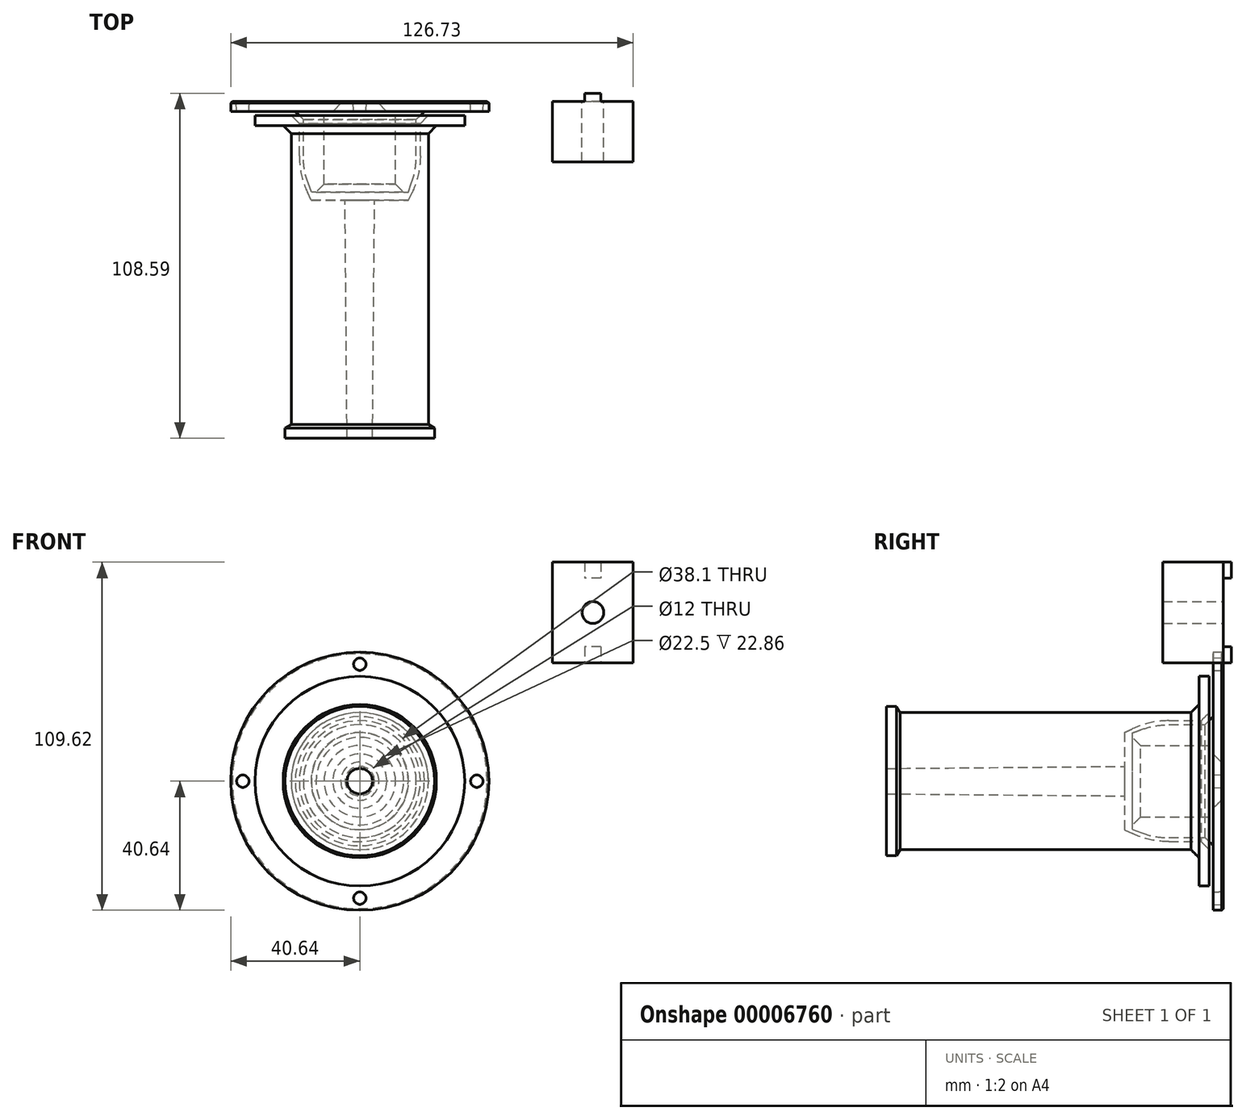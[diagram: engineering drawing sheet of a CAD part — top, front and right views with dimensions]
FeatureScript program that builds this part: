
annotation { "Feature Type Name" : "Feature", "Feature Type Description" : "" }
export const myFeature = defineFeature(function(context is Context, id is Id, definition is map)
    precondition{}
    {
        {
            var Q0;
            Q0=qCreatedBy(makeId("Front.planeOp"),FACE);
            var sketch = newSketch(context, id + "F0", { "sketchPlane" : qUnion([Q0])});
            skCircle(sketch, "E0", {"center": v(0, 0) * mm, "radius": 4 * mm, "construction": true});
            skCircle(sketch, "E1", {"center": v(0, 0) * mm, "radius": 11.25 * mm});
            skCircle(sketch, "E2", {"center": v(0, 0) * mm, "radius": 17.78 * mm});
            skCircle(sketch, "E3", {"center": v(0, 0) * mm, "radius": 6 * mm});
            skCircle(sketch, "E4", {"center": v(0, 0) * mm, "radius": 40.64 * mm});
            skSolve(sketch);
        }
        {
            var Q0;
            Q0=makeQuery(id+"F0.imprint","IMPRINT",FACE,{"disambiguationData":[TD([[makeQuery(id+"F0.imprint","IMPRINT",EDGE,{"derivedFrom":sQuery(id+"F0.wireOp",EDGE,"E1")}),-1.0]])]});
            var Q1;
            Q1=makeQuery(id+"F0.imprint","IMPRINT",FACE,{"disambiguationData":[TD([[makeQuery(id+"F0.imprint","IMPRINT",EDGE,{"derivedFrom":sQuery(id+"F0.wireOp",EDGE,"E1")}),1.0]])]});
            var Q2;
            Q2=makeQuery(id+"F0.imprint","IMPRINT",FACE,{"disambiguationData":[TD([[makeQuery(id+"F0.imprint","IMPRINT",EDGE,{"derivedFrom":sQuery(id+"F0.wireOp",EDGE,"E2")}),-1.0]])]});
            extrude(context, id + "F1", {"entities" : qUnion([Q0, Q1, Q2]), "depth" : 3.17 * mm, "offsetDistance" : 25.4 * mm});
        }
        {
            var Q0;
            Q0=makeQuery(id+"F0.imprint","IMPRINT",FACE,{"disambiguationData":[TD([[makeQuery(id+"F0.imprint","IMPRINT",EDGE,{"derivedFrom":sQuery(id+"F0.wireOp",EDGE,"E1")}),-1.0]])]});
            extrude(context, id + "F2", {"entities" : qUnion([Q0]), "operationType" : NewBodyOperationType.ADD, "depth" : 28.57 * mm, "offsetDistance" : 25.4 * mm});
        }
        {
            var Q0;
            Q0=makeQuery(id+"F2.opExtrude","CAP_EDGE",EDGE,{"disambiguationData":[OSD([sQuery(id+"F0.wireOp",EDGE,"E2")])],"isStart":false});
            chamfer(context, id + "F3", {"entities" : qUnion([Q0]), "chamferType" : ChamferType.OFFSET_ANGLE, "width" : 2.54 * mm, "oppositeDirection" : false, "angle" : 70 * degree, "tangentPropagation" : true});
        }
        {
            var Q0;
            {var subQ0=sQuery(id+"F0.wireOp",EDGE,"E2");Q0=makeQuery(id+"F3.opChamfer","BLEND_EDGE",EDGE,{"blendedFrom":[makeQuery(id+"F2.opExtrude","CAP_EDGE",EDGE,{"disambiguationData":[OSD([subQ0])],"isStart":false}),makeQuery(id+"F2.boolean.opBoolean","MERGE",FACE,{"derivedFrom":[makeQuery(id+"F1.opExtrude","SWEPT_FACE",FACE,{"disambiguationData":[OSD([subQ0])]}),makeQuery(id+"F2.opExtrude","SWEPT_FACE",FACE,{"disambiguationData":[OSD([subQ0])]})]})],"blendedInto":[makeQuery(id+"F2.boolean.opBoolean","MERGE",FACE,{"derivedFrom":[makeQuery(id+"F1.opExtrude","SWEPT_FACE",FACE,{"disambiguationData":[OSD([subQ0])]}),makeQuery(id+"F2.opExtrude","SWEPT_FACE",FACE,{"disambiguationData":[OSD([subQ0])]})]})]});}
            fillet(context, id + "F4", {"entities" : qUnion([Q0]), "radius" : 25.4 * mm, "tangentPropagation" : true, "allowEdgeOverflow" : false});
        }
        {
            var Q0;
            Q0=qCreatedBy(makeId("Top.planeOp"),FACE);
            var sketch = newSketch(context, id + "F5", { "sketchPlane" : qUnion([Q0])});
            skLineSegment(sketch, "E5", {"start": v(0, 0) * mm, "end": v(0, -48.11) * mm, "construction": true});
            skArc(sketch, "E6", {"start": v(16.5, -28.58) * mm, "mid": v(18.4, -22.99) * mm, "end": v(19.05, -17.12) * mm});
            skLineSegment(sketch, "E7", {"start": v(19.05, -17.12) * mm, "end": v(17.78, -17.12) * mm, "construction": true});
            skLineSegment(sketch, "E8", {"start": v(16.5, -28.58) * mm, "end": v(15.24, -28.58) * mm, "construction": true});
            skLineSegment(sketch, "E9", {"start": v(19.05, -17.12) * mm, "end": v(19.05, -4.45) * mm});
            skLineSegment(sketch, "E10", {"start": v(19.05, -4.45) * mm, "end": v(33.02, -4.45) * mm});
            skLineSegment(sketch, "E11", {"start": v(16.5, -28.58) * mm, "end": v(15.33, -31.12) * mm});
            skLineSegment(sketch, "E12", {"start": v(15.33, -31.12) * mm, "end": v(4.65, -31.12) * mm});
            skLineSegment(sketch, "E13", {"start": v(4.65, -31.11) * mm, "end": v(4, -106.05) * mm});
            skLineSegment(sketch, "E14", {"start": v(4, -106.05) * mm, "end": v(23.5, -106.05) * mm});
            skLineSegment(sketch, "E15", {"start": v(23.5, -106.05) * mm, "end": v(23.5, -102.87) * mm});
            skLineSegment(sketch, "E16", {"start": v(23.5, -102.87) * mm, "end": v(21.6, -101.77) * mm});
            skLineSegment(sketch, "E17", {"start": v(33.02, -4.45) * mm, "end": v(33.02, -7.62) * mm});
            skLineSegment(sketch, "E18", {"start": v(33.02, -7.62) * mm, "end": v(21.59, -7.62) * mm});
            skLineSegment(sketch, "E19", {"start": v(21.59, -7.62) * mm, "end": v(21.6, -101.77) * mm});
            skSolve(sketch);
        }
        {
            var Q0;
            {var subQ5=sQuery(id+"F5.wireOp",EDGE,"E9");Q0=makeQuery(id+"F5.imprint","IMPRINT",FACE,{"disambiguationData":[TD([[makeQuery(id+"F5.imprint","IMPRINT",EDGE,{"derivedFrom":subQ5}),-1.0]])]});}
            var Q1;
            Q1=sQuery(id+"F5.wireOp",EDGE,"E5");
            revolve(context, id + "F6", {"entities" : qUnion([Q0]), "axis" : qUnion([Q1]), "revolveType" : RevolveType.FULL});
        }
        {
            var Q0;
            Q0=makeQuery(id+"F2.opExtrude","CAP_EDGE",EDGE,{"disambiguationData":[OSD([sQuery(id+"F0.wireOp",EDGE,"E1")])],"isStart":false});
            var Q1;
            Q1=makeQuery(id+"F1.opExtrude","CAP_EDGE",EDGE,{"disambiguationData":[OSD([sQuery(id+"F0.wireOp",EDGE,"E3")])],"isStart":false});
            var Q2;
            Q2=makeQuery(id+"F6.opRevolve","SWEPT_EDGE",EDGE,{"disambiguationData":[OSD([sQuery(id+"F5.wireOp",EDGE,"E18"),sQuery(id+"F5.wireOp",EDGE,"E19")])]});
            var Q3;
            Q3=makeQuery(id+"F6.opRevolve","SWEPT_EDGE",EDGE,{"disambiguationData":[OSD([sQuery(id+"F5.wireOp",EDGE,"E9"),sQuery(id+"F5.wireOp",EDGE,"E10")])]});
            var Q4;
            Q4=makeQuery(id+"F2.boolean.opBoolean","INTERSECT",EDGE,{"derivedFrom":[makeQuery(id+"F1.opExtrude","CAP_FACE",FACE,{"disambiguationData":[OSD([sQuery(id+"F0.wireOp",EDGE,"E3"),sQuery(id+"F0.wireOp",EDGE,"E4")])],"isStart":false}),makeQuery(id+"F2.opExtrude","SWEPT_FACE",FACE,{"disambiguationData":[OSD([sQuery(id+"F0.wireOp",EDGE,"E2")])]})]});
            chamfer(context, id + "F7", {"entities" : qUnion([Q0, Q1, Q2, Q3, Q4]), "width" : 2.54 * mm, "tangentPropagation" : true});
        }
        {
            var Q0;
            Q0=qCreatedBy(makeId("Right.planeOp"),FACE);
            var sketch = newSketch(context, id + "F8", { "sketchPlane" : qUnion([Q0])});
            skLineSegment(sketch, "E20", {"start": v(0, 38.9) * mm, "end": v(-3.18, 38.77) * mm});
            skLineSegment(sketch, "E21", {"start": v(-3.18, 38.77) * mm, "end": v(-3.18, 36.83) * mm});
            skLineSegment(sketch, "E22", {"start": v(-3.18, 36.83) * mm, "end": v(0, 36.83) * mm});
            skLineSegment(sketch, "E23", {"start": v(0, 36.83) * mm, "end": v(0, 38.9) * mm});
            skLineSegment(sketch, "E24", {"start": v(-4.45, 33.02) * mm, "end": v(-7.62, 33.02) * mm});
            skLineSegment(sketch, "E25", {"start": v(-7.62, -33.02) * mm, "end": v(-4.45, -33.02) * mm});
            skLineSegment(sketch, "E26", {"start": v(-3.18, 40.64) * mm, "end": v(0, 40.64) * mm});
            skLineSegment(sketch, "E27", {"start": v(0, -40.64) * mm, "end": v(-3.18, -40.64) * mm});
            skLineSegment(sketch, "E28", {"start": v(-3.18, 40.64) * mm, "end": v(-3.18, 33.02) * mm, "construction": true});
            skSolve(sketch);
        }
        {
            var Q0;
            Q0=makeQuery(id+"F8.imprint","IMPRINT",FACE,{"disambiguationData":[TD([[makeQuery(id+"F8.imprint","IMPRINT",EDGE,{"derivedFrom":sQuery(id+"F8.wireOp",EDGE,"E20")}),1.0]])]});
            var Q1;
            Q1=sQuery(id+"F8.wireOp",EDGE,"E22");
            revolve(context, id + "F9", {"surfaceOperationType" : NewSurfaceOperationType.NEW, "entities" : qUnion([Q0]), "axis" : qUnion([Q1]), "revolveType" : RevolveType.FULL});
        }
        {
            var Q0;
            Q0=makeQuery(id+"F9.opRevolve","SWEPT_BODY",BODY,{"disambiguationData":[OSD([sQuery(id+"F8.wireOp",EDGE,"E20"),sQuery(id+"F8.wireOp",EDGE,"E21"),sQuery(id+"F8.wireOp",EDGE,"E22"),sQuery(id+"F8.wireOp",EDGE,"E23")])]});
            var Q1;
            Q1=makeQuery(id+"F1.opExtrude","SWEPT_FACE",FACE,{"disambiguationData":[OSD([sQuery(id+"F0.wireOp",EDGE,"E4")])]});
            circularPattern(context, id + "F10", {"entities" : qUnion([Q0]), "axis" : qUnion([Q1]), "angle" : 360 * degree, "instanceCount" : 4, "equalSpace" : true});
        }
        {
            var Q0;
            Q0=makeQuery(id+"F9.opRevolve","SWEPT_BODY",BODY,{"disambiguationData":[OSD([sQuery(id+"F8.wireOp",EDGE,"E20"),sQuery(id+"F8.wireOp",EDGE,"E21"),sQuery(id+"F8.wireOp",EDGE,"E22"),sQuery(id+"F8.wireOp",EDGE,"E23")])]});
            var Q1;
            Q1=makeQuery(id+"F10.opPattern","COPY",BODY,{"derivedFrom":makeQuery(id+"F9.opRevolve","SWEPT_BODY",BODY,{"disambiguationData":[OSD([sQuery(id+"F8.wireOp",EDGE,"E20"),sQuery(id+"F8.wireOp",EDGE,"E21"),sQuery(id+"F8.wireOp",EDGE,"E22"),sQuery(id+"F8.wireOp",EDGE,"E23")])]}),"instanceName":"1"});
            var Q2;
            Q2=makeQuery(id+"F10.opPattern","COPY",BODY,{"derivedFrom":makeQuery(id+"F9.opRevolve","SWEPT_BODY",BODY,{"disambiguationData":[OSD([sQuery(id+"F8.wireOp",EDGE,"E20"),sQuery(id+"F8.wireOp",EDGE,"E21"),sQuery(id+"F8.wireOp",EDGE,"E22"),sQuery(id+"F8.wireOp",EDGE,"E23")])]}),"instanceName":"2"});
            var Q3;
            Q3=makeQuery(id+"F10.opPattern","COPY",BODY,{"derivedFrom":makeQuery(id+"F9.opRevolve","SWEPT_BODY",BODY,{"disambiguationData":[OSD([sQuery(id+"F8.wireOp",EDGE,"E20"),sQuery(id+"F8.wireOp",EDGE,"E21"),sQuery(id+"F8.wireOp",EDGE,"E22"),sQuery(id+"F8.wireOp",EDGE,"E23")])]}),"instanceName":"3"});
            var Q4;
            Q4=makeQuery(id+"F1.opExtrude","SWEPT_BODY",BODY,{"disambiguationData":[OSD([sQuery(id+"F0.wireOp",EDGE,"E3"),sQuery(id+"F0.wireOp",EDGE,"E4")])]});
            booleanBodies(context, id + "F11", {"operationType" : BooleanOperationType.SUBTRACTION, "tools" : qUnion([Q0, Q1, Q2, Q3]), "targets" : qUnion([Q4])});
        }
        {
            var Q0;
            Q0=makeQuery(id+"F11.opBoolean","COPY",EDGE,{"derivedFrom":makeQuery(id+"F10.opPattern","COPY",EDGE,{"derivedFrom":makeQuery(id+"F9.opRevolve","SWEPT_EDGE",EDGE,{"disambiguationData":[OSD([sQuery(id+"F8.wireOp",EDGE,"E20"),sQuery(id+"F8.wireOp",EDGE,"E23")])]}),"instanceName":"1"})});
            var Q1;
            Q1=makeQuery(id+"F11.opBoolean","COPY",EDGE,{"derivedFrom":makeQuery(id+"F9.opRevolve","SWEPT_EDGE",EDGE,{"disambiguationData":[OSD([sQuery(id+"F8.wireOp",EDGE,"E20"),sQuery(id+"F8.wireOp",EDGE,"E23")])]})});
            var Q2;
            Q2=makeQuery(id+"F11.opBoolean","COPY",EDGE,{"derivedFrom":makeQuery(id+"F10.opPattern","COPY",EDGE,{"derivedFrom":makeQuery(id+"F9.opRevolve","SWEPT_EDGE",EDGE,{"disambiguationData":[OSD([sQuery(id+"F8.wireOp",EDGE,"E20"),sQuery(id+"F8.wireOp",EDGE,"E23")])]}),"instanceName":"3"})});
            var Q3;
            Q3=makeQuery(id+"F11.opBoolean","COPY",EDGE,{"derivedFrom":makeQuery(id+"F10.opPattern","COPY",EDGE,{"derivedFrom":makeQuery(id+"F9.opRevolve","SWEPT_EDGE",EDGE,{"disambiguationData":[OSD([sQuery(id+"F8.wireOp",EDGE,"E20"),sQuery(id+"F8.wireOp",EDGE,"E23")])]}),"instanceName":"2"})});
            var Q4;
            Q4=makeQuery(id+"F1.opExtrude","CAP_EDGE",EDGE,{"disambiguationData":[OSD([sQuery(id+"F0.wireOp",EDGE,"E4")])],"isStart":true});
            chamfer(context, id + "F12", {"entities" : qUnion([Q0, Q1, Q2, Q3, Q4]), "width" : 0.5 * mm, "tangentPropagation" : true});
        }
        {
            var Q0;
            Q0=qCreatedBy(makeId("Front.planeOp"),FACE);
            var sketch = newSketch(context, id + "F13", { "sketchPlane" : qUnion([Q0])});
            skLineSegment(sketch, "E29.bottom", {"start": v(86.09, 37.23) * mm, "end": v(60.69, 37.23) * mm});
            skLineSegment(sketch, "E29.top", {"start": v(86.09, 68.98) * mm, "end": v(60.69, 68.98) * mm});
            skLineSegment(sketch, "E29.left", {"start": v(86.09, 37.23) * mm, "end": v(86.09, 68.98) * mm});
            skLineSegment(sketch, "E29.right", {"start": v(60.69, 37.23) * mm, "end": v(60.69, 68.98) * mm});
            skPoint(sketch, "E29.middle", {"position": v(73.39, 53.1) * mm});
            skCircle(sketch, "E30", {"center": v(73.39, 53.1) * mm, "radius": 3.43 * mm});
            skLineSegment(sketch, "E31", {"start": v(73.39, 66.44) * mm, "end": v(73.39, 39.77) * mm, "construction": true});
            skLineSegment(sketch, "E32.bottom", {"start": v(75.93, 68.98) * mm, "end": v(70.85, 68.98) * mm});
            skLineSegment(sketch, "E32.top", {"start": v(75.93, 63.9) * mm, "end": v(70.85, 63.9) * mm});
            skLineSegment(sketch, "E32.left", {"start": v(75.93, 68.98) * mm, "end": v(75.93, 63.9) * mm});
            skLineSegment(sketch, "E32.right", {"start": v(70.85, 68.98) * mm, "end": v(70.85, 63.9) * mm});
            skPoint(sketch, "E32.middle", {"position": v(73.39, 66.44) * mm});
            skLineSegment(sketch, "E33.bottom", {"start": v(75.93, 42.3) * mm, "end": v(70.85, 42.3) * mm});
            skLineSegment(sketch, "E33.top", {"start": v(75.93, 37.23) * mm, "end": v(70.85, 37.23) * mm});
            skLineSegment(sketch, "E33.left", {"start": v(75.93, 42.3) * mm, "end": v(75.93, 37.23) * mm});
            skLineSegment(sketch, "E33.right", {"start": v(70.85, 42.3) * mm, "end": v(70.85, 37.23) * mm});
            skPoint(sketch, "E33.middle", {"position": v(73.39, 39.77) * mm});
            skSolve(sketch);
        }
        {
            var Q0;
            {var subQ2=sQuery(id+"F13.wireOp",EDGE,"E29.left");Q0=makeQuery(id+"F13.imprint","IMPRINT",FACE,{"disambiguationData":[TD([[makeQuery(id+"F13.imprint","IMPRINT",EDGE,{"derivedFrom":subQ2}),1.0]])]});}
            var Q1;
            Q1=makeQuery(id+"F13.imprint","IMPRINT",FACE,{"disambiguationData":[TD([[makeQuery(id+"F13.imprint","IMPRINT",EDGE,{"derivedFrom":sQuery(id+"F13.wireOp",EDGE,"E32.top")}),-1.0]])]});
            var Q2;
            Q2=makeQuery(id+"F13.imprint","IMPRINT",FACE,{"disambiguationData":[TD([[makeQuery(id+"F13.imprint","IMPRINT",EDGE,{"derivedFrom":sQuery(id+"F13.wireOp",EDGE,"E33.bottom")}),1.0]])]});
            extrude(context, id + "F14", {"entities" : qUnion([Q0, Q1, Q2]), "depth" : 19.05 * mm, "offsetDistance" : 25.4 * mm});
        }
        {
            var Q0;
            Q0=makeQuery(id+"F13.imprint","IMPRINT",FACE,{"disambiguationData":[TD([[makeQuery(id+"F13.imprint","IMPRINT",EDGE,{"derivedFrom":sQuery(id+"F13.wireOp",EDGE,"E32.top")}),-1.0]])]});
            var Q1;
            Q1=makeQuery(id+"F13.imprint","IMPRINT",FACE,{"disambiguationData":[TD([[makeQuery(id+"F13.imprint","IMPRINT",EDGE,{"derivedFrom":sQuery(id+"F13.wireOp",EDGE,"E33.bottom")}),1.0]])]});
            extrude(context, id + "F15", {"entities" : qUnion([Q0, Q1]), "operationType" : NewBodyOperationType.ADD, "oppositeDirection" : true, "depth" : 2.54 * mm, "offsetDistance" : 25.4 * mm});
        }
    });
